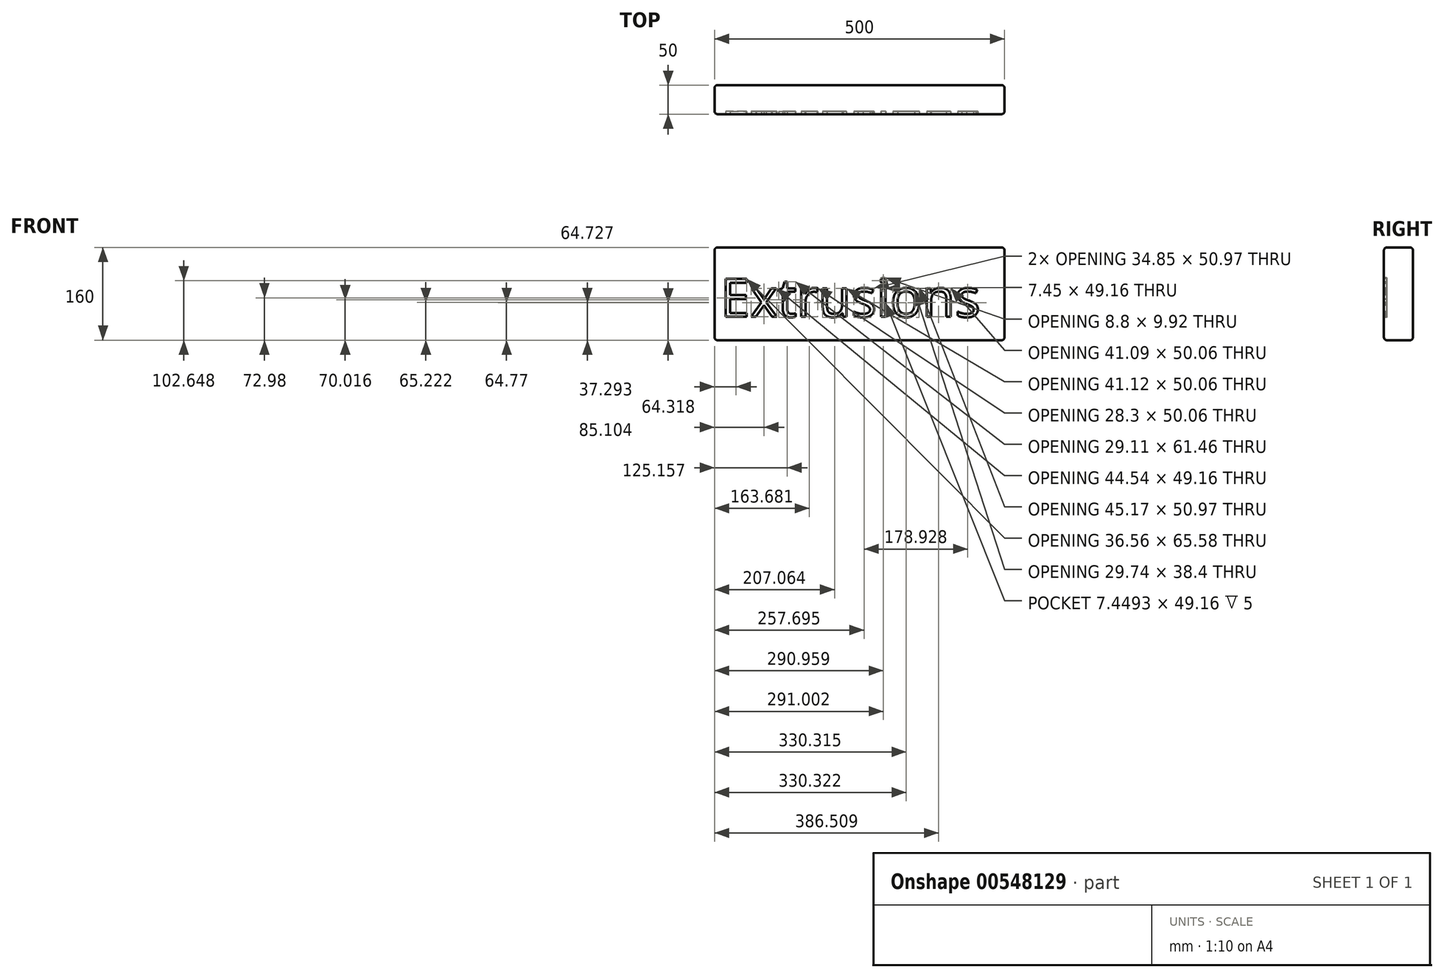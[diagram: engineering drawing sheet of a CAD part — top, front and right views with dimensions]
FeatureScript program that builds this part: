
annotation { "Feature Type Name" : "Feature", "Feature Type Description" : "" }
export const myFeature = defineFeature(function(context is Context, id is Id, definition is map)
    precondition{}
    {
        {
            var Q0;
            Q0=qCreatedBy(makeId("Top.planeOp"),FACE);
            var sketch = newSketch(context, id + "F0", { "sketchPlane" : qUnion([Q0])});
            skLineSegment(sketch, "E0.bottom", {"start": v(0, 0) * mm, "end": v(-500, 0) * mm});
            skLineSegment(sketch, "E0.top", {"start": v(0, -50) * mm, "end": v(-500, -50) * mm});
            skLineSegment(sketch, "E0.left", {"start": v(0, 0) * mm, "end": v(0, -50) * mm});
            skLineSegment(sketch, "E0.right", {"start": v(-500, 0) * mm, "end": v(-500, -50) * mm});
            skSolve(sketch);
        }
        {
            var Q0;
            Q0=makeQuery(id+"F0.imprint","IMPRINT",FACE,{"disambiguationData":[TD([[makeQuery(id+"F0.imprint","IMPRINT",EDGE,{"derivedFrom":sQuery(id+"F0.wireOp",EDGE,"E0.bottom")}),1.0]])]});
            extrude(context, id + "F1", {"entities" : qUnion([Q0]), "depth" : 160 * mm, "offsetDistance" : 25 * mm});
        }
        {
            var Q0;
            Q0=makeQuery(id+"F1.opExtrude","SWEPT_EDGE",EDGE,{"disambiguationData":[OSD([sQuery(id+"F0.wireOp",EDGE,"E0.top"),sQuery(id+"F0.wireOp",EDGE,"E0.left")])]});
            var Q1;
            Q1=makeQuery(id+"F1.opExtrude","SWEPT_EDGE",EDGE,{"disambiguationData":[OSD([sQuery(id+"F0.wireOp",EDGE,"E0.bottom"),sQuery(id+"F0.wireOp",EDGE,"E0.left")])]});
            var Q2;
            Q2=makeQuery(id+"F1.opExtrude","CAP_FACE",FACE,{"disambiguationData":[OSD([sQuery(id+"F0.wireOp",EDGE,"E0.bottom"),sQuery(id+"F0.wireOp",EDGE,"E0.top"),sQuery(id+"F0.wireOp",EDGE,"E0.left"),sQuery(id+"F0.wireOp",EDGE,"E0.right")])],"isStart":false});
            var Q3;
            Q3=makeQuery(id+"F1.opExtrude","CAP_EDGE",EDGE,{"disambiguationData":[OSD([sQuery(id+"F0.wireOp",EDGE,"E0.top")])],"isStart":false});
            var Q4;
            Q4=makeQuery(id+"F1.opExtrude","SWEPT_FACE",FACE,{"disambiguationData":[OSD([sQuery(id+"F0.wireOp",EDGE,"E0.top")])]});
            var Q5;
            Q5=makeQuery(id+"F1.opExtrude","SWEPT_FACE",FACE,{"disambiguationData":[OSD([sQuery(id+"F0.wireOp",EDGE,"E0.right")])]});
            var Q6;
            Q6=makeQuery(id+"F1.opExtrude","SWEPT_FACE",FACE,{"disambiguationData":[OSD([sQuery(id+"F0.wireOp",EDGE,"E0.bottom")])]});
            var Q7;
            Q7=makeQuery(id+"F1.opExtrude","CAP_FACE",FACE,{"disambiguationData":[OSD([sQuery(id+"F0.wireOp",EDGE,"E0.bottom"),sQuery(id+"F0.wireOp",EDGE,"E0.top"),sQuery(id+"F0.wireOp",EDGE,"E0.left"),sQuery(id+"F0.wireOp",EDGE,"E0.right")])],"isStart":true});
            fillet(context, id + "F2", {"entities" : qUnion([Q0, Q1, Q2, Q3, Q4, Q5, Q6, Q7]), "radius" : 5 * mm, "tangentPropagation" : true, "allowEdgeOverflow" : false});
        }
        {
            var Q0;
            Q0=makeQuery(id+"F1.opExtrude","SWEPT_FACE",FACE,{"disambiguationData":[OSD([sQuery(id+"F0.wireOp",EDGE,"E0.top")])]});
            var sketch = newSketch(context, id + "F3", { "sketchPlane" : qUnion([Q0])});
            skText(sketch, "E1", { "text": "Extrusions\n", "fontName": "OpenSans-Regular.ttf"});
            const initialGuessF3  = {"E1": [-0.49, 0.04019, 1, 0, 0.06614]};
            skSetInitialGuess(sketch, initialGuessF3);
            skSolve(sketch);
        }
        {
            var Q0;
            Q0 = qSketchRegion(id + "F3", true);
            extrude(context, id + "F4", {"entities" : qUnion([Q0]), "operationType" : NewBodyOperationType.REMOVE, "oppositeDirection" : true, "depth" : 5 * mm, "offsetDistance" : 25 * mm});
        }
    });
